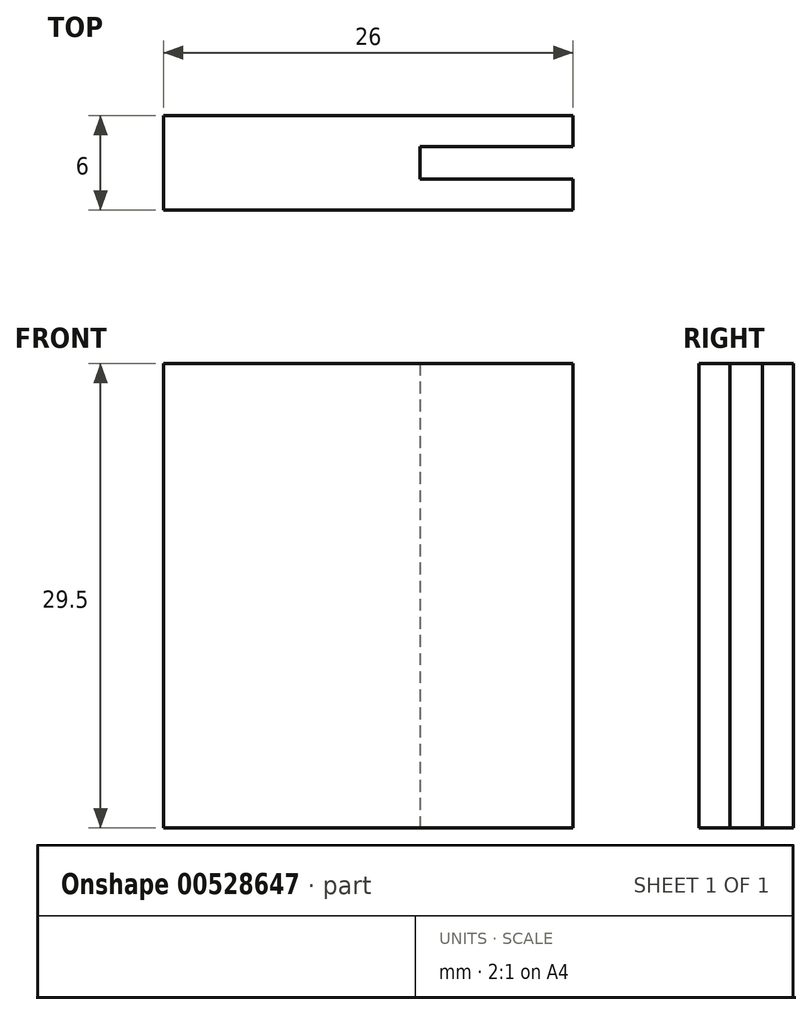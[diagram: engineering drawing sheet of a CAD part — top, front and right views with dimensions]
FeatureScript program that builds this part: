
annotation { "Feature Type Name" : "Feature", "Feature Type Description" : "" }
export const myFeature = defineFeature(function(context is Context, id is Id, definition is map)
    precondition{}
    {
        {
            var Q0;
            Q0=qCreatedBy(makeId("Top.planeOp"),FACE);
            var sketch = newSketch(context, id + "F0", { "sketchPlane" : qUnion([Q0])});
            skLineSegment(sketch, "E0.bottom", {"start": v(0, 0) * mm, "end": v(26, 0) * mm});
            skLineSegment(sketch, "E0.top", {"start": v(0, 6) * mm, "end": v(26, 6) * mm});
            skLineSegment(sketch, "E0.left", {"start": v(0, 0) * mm, "end": v(0, 6) * mm});
            skLineSegment(sketch, "E0.right", {"start": v(26, 0) * mm, "end": v(26, 1.97) * mm});
            skLineSegment(sketch, "E1", {"start": v(26, 4.03) * mm, "end": v(16.27, 4.03) * mm});
            skLineSegment(sketch, "E2", {"start": v(16.27, 4.03) * mm, "end": v(16.27, 1.97) * mm});
            skLineSegment(sketch, "E3", {"start": v(16.27, 1.97) * mm, "end": v(26, 1.97) * mm});
            skLineSegment(sketch, "E4.trimOffspring", {"start": v(26, 4.03) * mm, "end": v(26, 6) * mm});
            skSolve(sketch);
        }
        {
            var Q0;
            Q0 = qSketchRegion(id + "F0", true);
            extrude(context, id + "F1", {"entities" : qUnion([Q0]), "depth" : 29.5 * mm, "offsetDistance" : 25 * mm});
        }
    });
